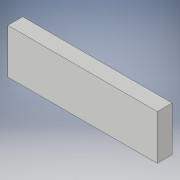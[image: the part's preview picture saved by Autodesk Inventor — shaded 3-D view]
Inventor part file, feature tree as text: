
AUTODESK INVENTOR PART (.ipt)
format: ipt  version: 2018 (Build 220112000, 112)  size: 87,552 bytes
history: native  units: in
note: dims shown in document units (in); Inventor stores cm internally (conversion verified against a paired STEP export)
features: extrude x1, sketch x1
ambient origin geometry x8: Origin, YZ Plane, XZ Plane, XY Plane, X Axis, Y Axis, Z Axis, Center Point
bodies: Solid1 (feature_tree)
feature tree (2):
  extrude  "Extrusion1"  Depth=0.5906in
  sketch  "Sketch1"  dims[d0=1.9685in d1=0.5906in d2=0.1969in d3=0.0in]
